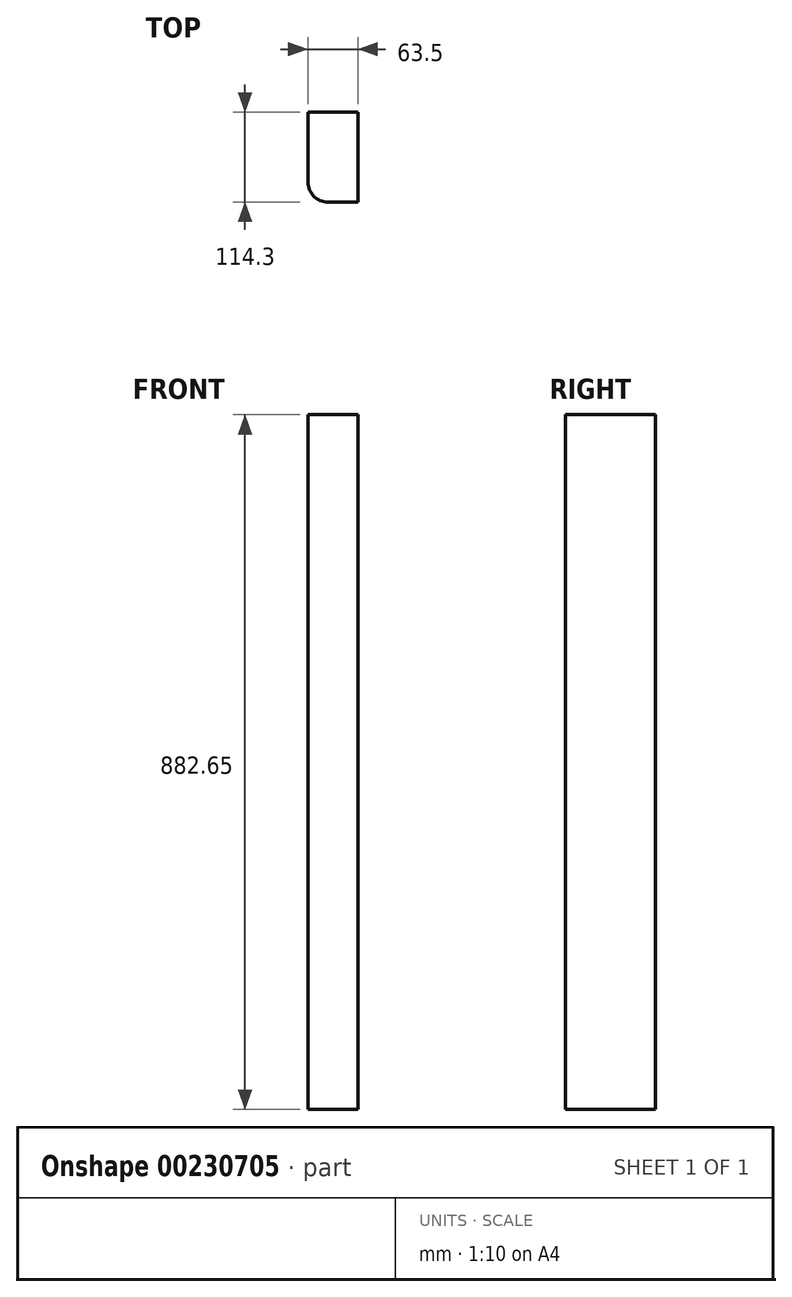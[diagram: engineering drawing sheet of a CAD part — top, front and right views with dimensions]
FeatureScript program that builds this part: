
annotation { "Feature Type Name" : "Feature", "Feature Type Description" : "" }
export const myFeature = defineFeature(function(context is Context, id is Id, definition is map)
    precondition{}
    {
        {
            var Q0;
            Q0=qCreatedBy(makeId("Top.planeOp"),FACE);
            var sketch = newSketch(context, id + "F0", { "sketchPlane" : qUnion([Q0])});
            skLineSegment(sketch, "E0.bottom", {"start": v(12.42, -13.96) * mm, "end": v(-51.08, -13.96) * mm});
            skLineSegment(sketch, "E0.top", {"start": v(12.42, 100.34) * mm, "end": v(-51.08, 100.34) * mm});
            skLineSegment(sketch, "E0.left", {"start": v(12.42, -13.96) * mm, "end": v(12.42, 100.34) * mm});
            skLineSegment(sketch, "E0.right", {"start": v(-51.08, -13.96) * mm, "end": v(-51.08, 100.34) * mm});
            skPoint(sketch, "E0.middle", {"position": v(-19.33, 43.2) * mm});
            skSolve(sketch);
        }
        {
            var Q0;
            Q0=makeQuery(id+"F0.imprint","IMPRINT",FACE,{"disambiguationData":[TD([[makeQuery(id+"F0.imprint","IMPRINT",EDGE,{"derivedFrom":sQuery(id+"F0.wireOp",EDGE,"E0.bottom")}),-1.0]])]});
            extrude(context, id + "F1", {"entities" : qUnion([Q0]), "oppositeDirection" : true, "depth" : 882.65 * mm});
        }
        {
            var Q0;
            Q0=makeQuery(id+"F1.opExtrude","SWEPT_EDGE",EDGE,{"disambiguationData":[OSD([sQuery(id+"F0.wireOp",EDGE,"E0.bottom"),sQuery(id+"F0.wireOp",EDGE,"E0.right")])]});
            fillet(context, id + "F2", {"entities" : qUnion([Q0]), "radius" : 25.4 * mm, "tangentPropagation" : true, "allowEdgeOverflow" : false});
        }
    });
